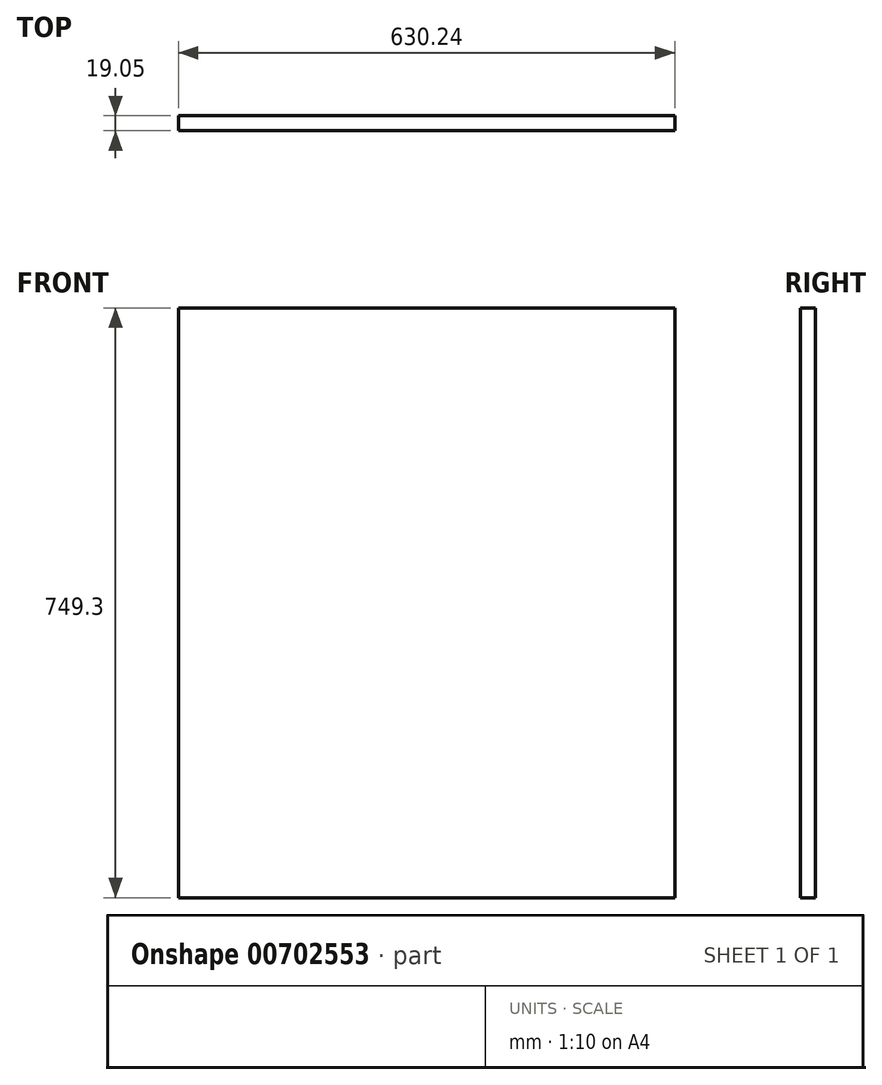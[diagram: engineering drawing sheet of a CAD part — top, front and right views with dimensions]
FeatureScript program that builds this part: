
annotation { "Feature Type Name" : "Feature", "Feature Type Description" : "" }
export const myFeature = defineFeature(function(context is Context, id is Id, definition is map)
    precondition{}
    {
        {
            var Q0;
            Q0=qCreatedBy(makeId("Front.planeOp"),FACE);
            var sketch = newSketch(context, id + "F0", { "sketchPlane" : qUnion([Q0])});
            skLineSegment(sketch, "E0.bottom", {"start": v(0, 0) * mm, "end": v(630.24, 0) * mm});
            skLineSegment(sketch, "E0.top", {"start": v(0, 749.3) * mm, "end": v(630.24, 749.3) * mm});
            skLineSegment(sketch, "E0.left", {"start": v(0, 0) * mm, "end": v(0, 749.3) * mm});
            skLineSegment(sketch, "E0.right", {"start": v(630.24, 0) * mm, "end": v(630.24, 749.3) * mm});
            skSolve(sketch);
        }
        {
            var Q0;
            Q0 = qSketchRegion(id + "F0", true);
            extrude(context, id + "F1", {"entities" : qUnion([Q0]), "depth" : 19.05 * mm, "offsetDistance" : 25.4 * mm});
        }
    });
